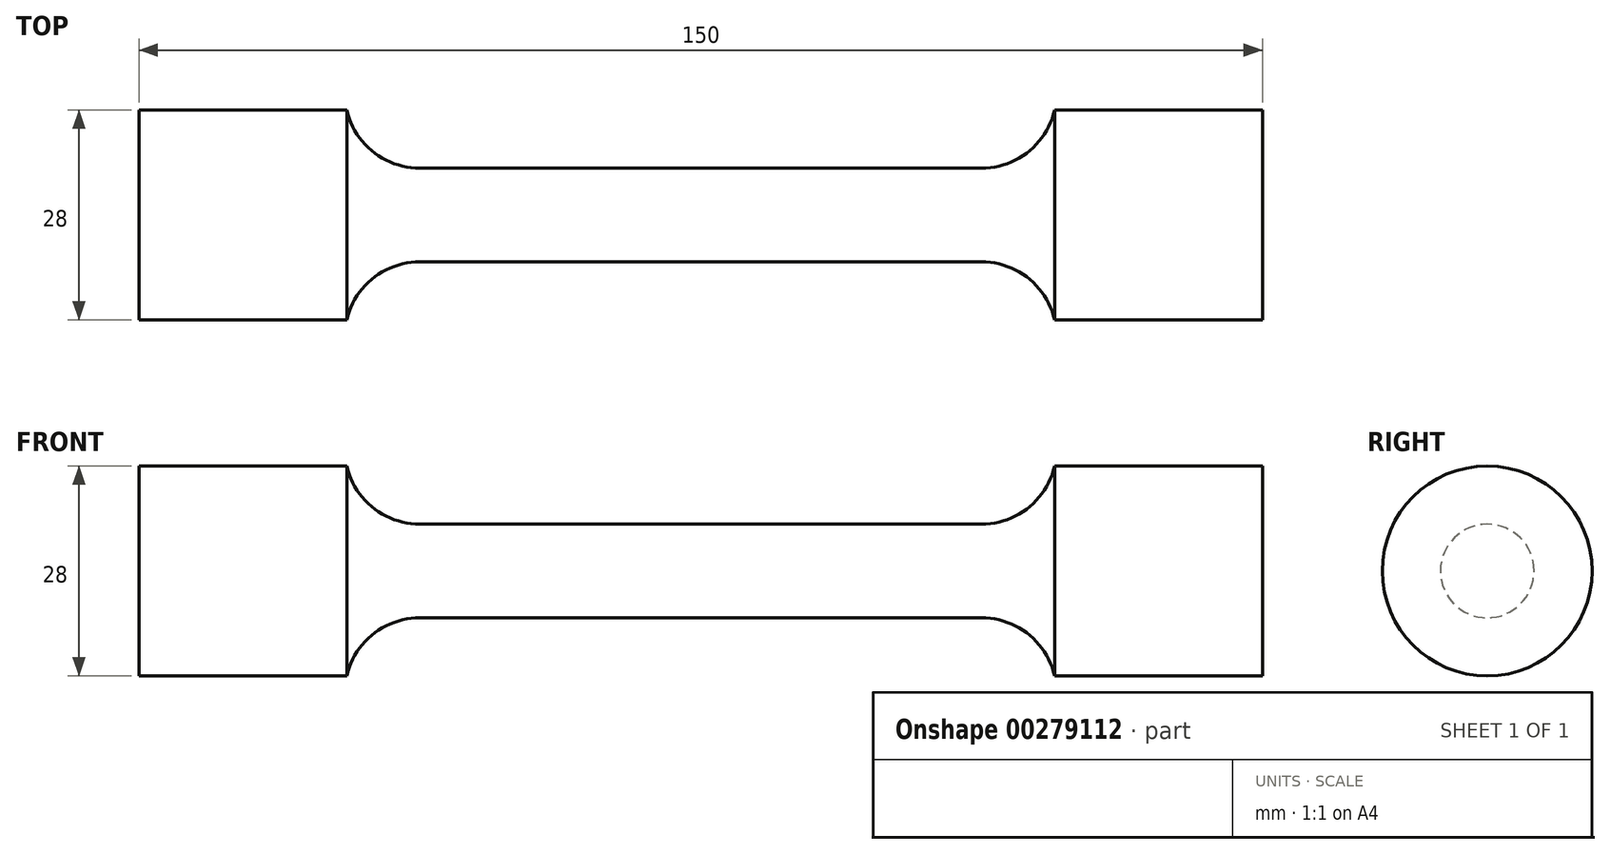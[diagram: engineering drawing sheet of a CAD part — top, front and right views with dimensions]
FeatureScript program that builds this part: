
annotation { "Feature Type Name" : "Feature", "Feature Type Description" : "" }
export const myFeature = defineFeature(function(context is Context, id is Id, definition is map)
    precondition{}
    {
        {
            var Q0;
            Q0=qCreatedBy(makeId("Front.planeOp"),FACE);
            var sketch = newSketch(context, id + "F0", { "sketchPlane" : qUnion([Q0])});
            skLineSegment(sketch, "E0", {"start": v(0, 6.25) * mm, "end": v(37.5, 6.25) * mm});
            skArc(sketch, "E1", {"start": v(37.5, 6.25) * mm, "mid": v(43.72, 8.42) * mm, "end": v(47.24, 14) * mm});
            skLineSegment(sketch, "E2", {"start": v(47.24, 14) * mm, "end": v(75, 14) * mm});
            skLineSegment(sketch, "E3", {"start": v(75, 14) * mm, "end": v(75, 0) * mm});
            skLineSegment(sketch, "E4", {"start": v(75, 0) * mm, "end": v(0, 0) * mm});
            skLineSegment(sketch, "E5.MirrorCS", {"start": v(0, 6.25) * mm, "end": v(-37.5, 6.25) * mm});
            skLineSegment(sketch, "E6.MirrorCS", {"start": v(-75, 0) * mm, "end": v(0, 0) * mm});
            skLineSegment(sketch, "E7.MirrorCS", {"start": v(-47.24, 14) * mm, "end": v(-75, 14) * mm});
            skLineSegment(sketch, "E8.MirrorCS", {"start": v(-75, 14) * mm, "end": v(-75, 0) * mm});
            skArc(sketch, "E9.MirrorCS", {"start": v(-37.5, 6.25) * mm, "mid": v(-43.72, 8.42) * mm, "end": v(-47.24, 14) * mm});
            skSolve(sketch);
        }
        {
            var Q0;
            Q0=makeQuery(id+"F0.imprint","IMPRINT",FACE,{"disambiguationData":[TD([[makeQuery(id+"F0.imprint","IMPRINT",EDGE,{"derivedFrom":sQuery(id+"F0.wireOp",EDGE,"E0")}),-1.0]])]});
            var Q1;
            Q1=sQuery(id+"F0.wireOp",EDGE,"E6.MirrorCS");
            revolve(context, id + "F1", {"entities" : qUnion([Q0]), "axis" : qUnion([Q1]), "revolveType" : RevolveType.FULL});
        }
    });
